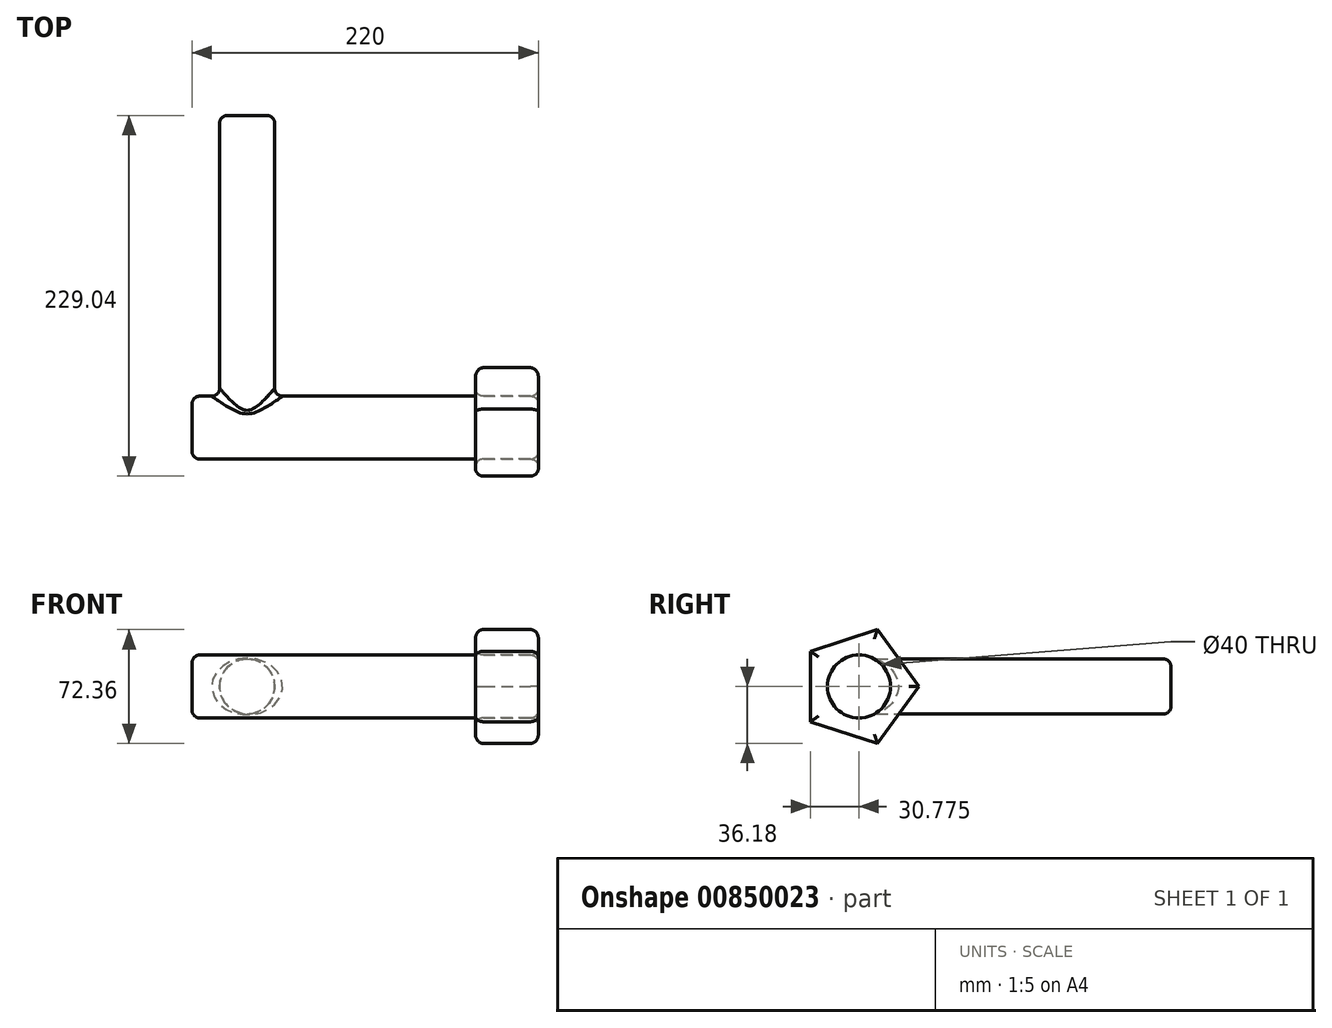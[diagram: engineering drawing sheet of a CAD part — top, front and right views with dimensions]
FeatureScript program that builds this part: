
annotation { "Feature Type Name" : "Feature", "Feature Type Description" : "" }
export const myFeature = defineFeature(function(context is Context, id is Id, definition is map)
    precondition{}
    {
        {
            var Q0;
            Q0=qCreatedBy(makeId("Front.planeOp"),FACE);
            var sketch = newSketch(context, id + "F0", { "sketchPlane" : qUnion([Q0])});
            skCircle(sketch, "E0", {"center": v(0, 0) * mm, "radius": 17.5 * mm});
            skSolve(sketch);
        }
        {
            var Q0;
            Q0=makeQuery(id+"F0.imprint","IMPRINT",FACE,{"disambiguationData":[TD([[makeQuery(id+"F0.imprint","IMPRINT",EDGE,{"derivedFrom":sQuery(id+"F0.wireOp",EDGE,"E0")}),1.0]])]});
            extrude(context, id + "F1", {"entities" : qUnion([Q0]), "depth" : 200 * mm, "offsetDistance" : 25 * mm});
        }
        {
            var Q0;
            Q0=qCreatedBy(makeId("Right.planeOp"),FACE);
            var sketch = newSketch(context, id + "F2", { "sketchPlane" : qUnion([Q0])});
            skCircle(sketch, "E1", {"center": v(-198.26, 0) * mm, "radius": 20 * mm});
            skSolve(sketch);
        }
        {
            var Q0;
            Q0 = qSketchRegion(id + "F2", true);
            extrude(context, id + "F3", {"entities" : qUnion([Q0]), "operationType" : NewBodyOperationType.ADD, "endBound" : BoundingType.SYMMETRIC, "depth" : 70 * mm, "offsetDistance" : 25 * mm});
        }
        {
            var Q0;
            Q0=makeQuery(id+"F3.opExtrude","CAP_FACE",FACE,{"disambiguationData":[OSD([sQuery(id+"F2.wireOp",EDGE,"E1")])],"isStart":false});
            extrude(context, id + "F4", {"entities" : qUnion([Q0]), "operationType" : NewBodyOperationType.ADD, "depth" : 150 * mm, "offsetDistance" : 25 * mm});
        }
        {
            var Q0;
            Q0=makeQuery(id+"F4.opExtrude","CAP_FACE",FACE,{"disambiguationData":[OSD([sQuery(id+"F2.wireOp",EDGE,"E1")])],"isStart":false});
            var sketch = newSketch(context, id + "F5", { "sketchPlane" : qUnion([Q0])});
            skCircle(sketch, "E2.cCircle", {"center": v(-198.26, 0) * mm, "radius": 30.78 * mm, "construction": true});
            skLineSegment(sketch, "E2.0", {"start": v(-186.5, 36.18) * mm, "end": v(-160.22, 0) * mm});
            skLineSegment(sketch, "E2.1", {"start": v(-160.22, 0) * mm, "end": v(-186.5, -36.18) * mm});
            skLineSegment(sketch, "E2.2", {"start": v(-186.5, -36.18) * mm, "end": v(-229.04, -22.36) * mm});
            skLineSegment(sketch, "E2.3", {"start": v(-229.04, -22.36) * mm, "end": v(-229.04, 22.36) * mm});
            skLineSegment(sketch, "E2.4", {"start": v(-229.04, 22.36) * mm, "end": v(-186.5, 36.18) * mm});
            skPoint(sketch, "E2.0.midPoint", {"position": v(-173.36, 18.1) * mm});
            skSolve(sketch);
        }
        {
            var Q0;
            Q0=makeQuery(id+"F5.imprint","IMPRINT",FACE,{"disambiguationData":[TD([[makeQuery(id+"F5.imprint","IMPRINT",EDGE,{"derivedFrom":sQuery(id+"F5.wireOp",EDGE,"E2.0")}),-1.0]])]});
            extrude(context, id + "F6", {"entities" : qUnion([Q0]), "oppositeDirection" : true, "depth" : 40 * mm, "offsetDistance" : 25 * mm});
        }
        {
            var Q0;
            Q0=makeQuery(id+"F1.opExtrude","SWEPT_FACE",FACE,{"disambiguationData":[OSD([sQuery(id+"F0.wireOp",EDGE,"E0")])]});
            var Q1;
            {var subQ0=sQuery(id+"F2.wireOp",EDGE,"E1");Q1=makeQuery(id+"F4.boolean.opBoolean","MERGE",FACE,{"derivedFrom":[makeQuery(id+"F3.opExtrude","SWEPT_FACE",FACE,{"disambiguationData":[OSD([subQ0])]}),makeQuery(id+"F4.opExtrude","SWEPT_FACE",FACE,{"disambiguationData":[OSD([subQ0])]})]});}
            var Q2;
            Q2=makeQuery(id+"F6.opExtrude","CAP_FACE",FACE,{"disambiguationData":[OSD([sQuery(id+"F2.wireOp",EDGE,"E1"),sQuery(id+"F5.wireOp",EDGE,"E2.0"),sQuery(id+"F5.wireOp",EDGE,"E2.1"),sQuery(id+"F5.wireOp",EDGE,"E2.2"),sQuery(id+"F5.wireOp",EDGE,"E2.3"),sQuery(id+"F5.wireOp",EDGE,"E2.4")])],"isStart":true});
            var Q3;
            Q3=makeQuery(id+"F6.opExtrude","CAP_FACE",FACE,{"disambiguationData":[OSD([sQuery(id+"F2.wireOp",EDGE,"E1"),sQuery(id+"F5.wireOp",EDGE,"E2.0"),sQuery(id+"F5.wireOp",EDGE,"E2.1"),sQuery(id+"F5.wireOp",EDGE,"E2.2"),sQuery(id+"F5.wireOp",EDGE,"E2.3"),sQuery(id+"F5.wireOp",EDGE,"E2.4")])],"isStart":false});
            var Q4;
            Q4=makeQuery(id+"F4.opExtrude","CAP_EDGE",EDGE,{"disambiguationData":[OSD([sQuery(id+"F2.wireOp",EDGE,"E1")])],"isStart":false});
            fillet(context, id + "F7", {"entities" : qUnion([Q0, Q1, Q2, Q3, Q4]), "radius" : 5 * mm, "tangentPropagation" : true, "allowEdgeOverflow" : false});
        }
    });
